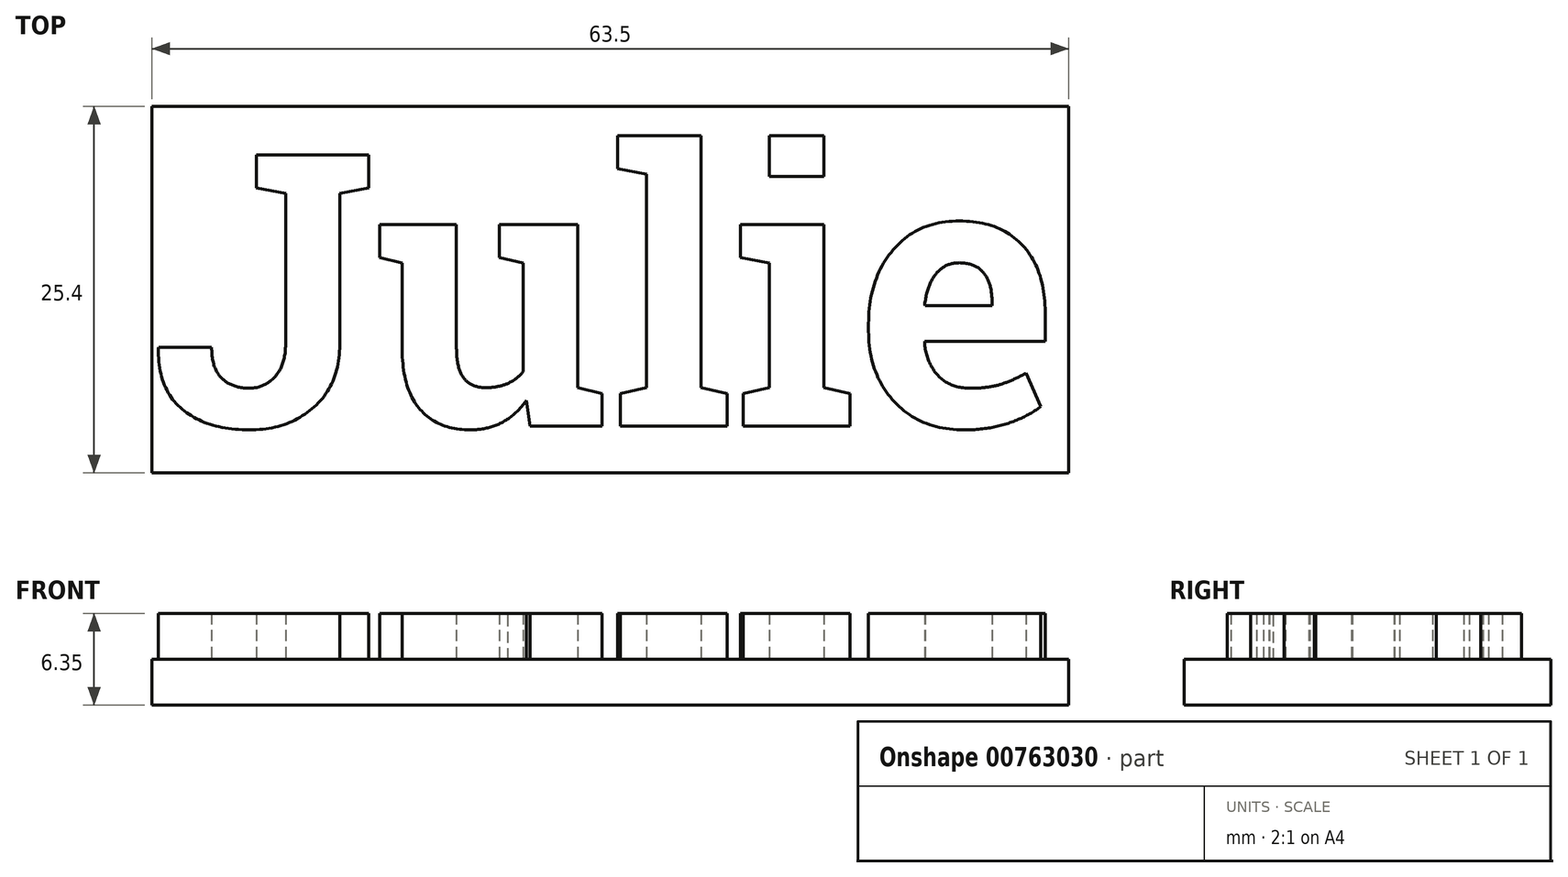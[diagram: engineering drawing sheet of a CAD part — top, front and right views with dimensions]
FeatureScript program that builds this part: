
annotation { "Feature Type Name" : "Feature", "Feature Type Description" : "" }
export const myFeature = defineFeature(function(context is Context, id is Id, definition is map)
    precondition{}
    {
        {
            var Q0;
            Q0=qCreatedBy(makeId("Top.planeOp"),FACE);
            var sketch = newSketch(context, id + "F0", { "sketchPlane" : qUnion([Q0])});
            skLineSegment(sketch, "E0.bottom", {"start": v(0, 0) * mm, "end": v(63.5, 0) * mm});
            skLineSegment(sketch, "E0.top", {"start": v(0, 25.4) * mm, "end": v(63.5, 25.4) * mm});
            skLineSegment(sketch, "E0.left", {"start": v(0, 0) * mm, "end": v(0, 25.4) * mm});
            skLineSegment(sketch, "E0.right", {"start": v(63.5, 0) * mm, "end": v(63.5, 25.4) * mm});
            skSolve(sketch);
        }
        {
            var Q0;
            Q0=makeQuery(id+"F0.imprint","IMPRINT",FACE,{"disambiguationData":[TD([[makeQuery(id+"F0.imprint","IMPRINT",EDGE,{"derivedFrom":sQuery(id+"F0.wireOp",EDGE,"E0.bottom")}),1.0]])]});
            extrude(context, id + "F1", {"entities" : qUnion([Q0]), "depth" : 3.17 * mm, "offsetDistance" : 25.4 * mm});
        }
        {
            var Q0;
            Q0=makeQuery(id+"F1.opExtrude","CAP_FACE",FACE,{"disambiguationData":[OSD([sQuery(id+"F0.wireOp",EDGE,"E0.bottom"),sQuery(id+"F0.wireOp",EDGE,"E0.top"),sQuery(id+"F0.wireOp",EDGE,"E0.left"),sQuery(id+"F0.wireOp",EDGE,"E0.right")])],"isStart":false});
            var sketch = newSketch(context, id + "F2", { "sketchPlane" : qUnion([Q0])});
            skText(sketch, "E1", { "text": "Julie", "fontName": "RobotoSlab-Bold.ttf"});
            const initialGuessF2  = {"E1": [0, 0.00325, 1, 0, 0.01901]};
            skSetInitialGuess(sketch, initialGuessF2);
            skSolve(sketch);
        }
        {
            var Q0;
            Q0 = qSketchRegion(id + "F2", true);
            extrude(context, id + "F3", {"entities" : qUnion([Q0]), "operationType" : NewBodyOperationType.ADD, "depth" : 3.17 * mm, "offsetDistance" : 25.4 * mm});
        }
    });
